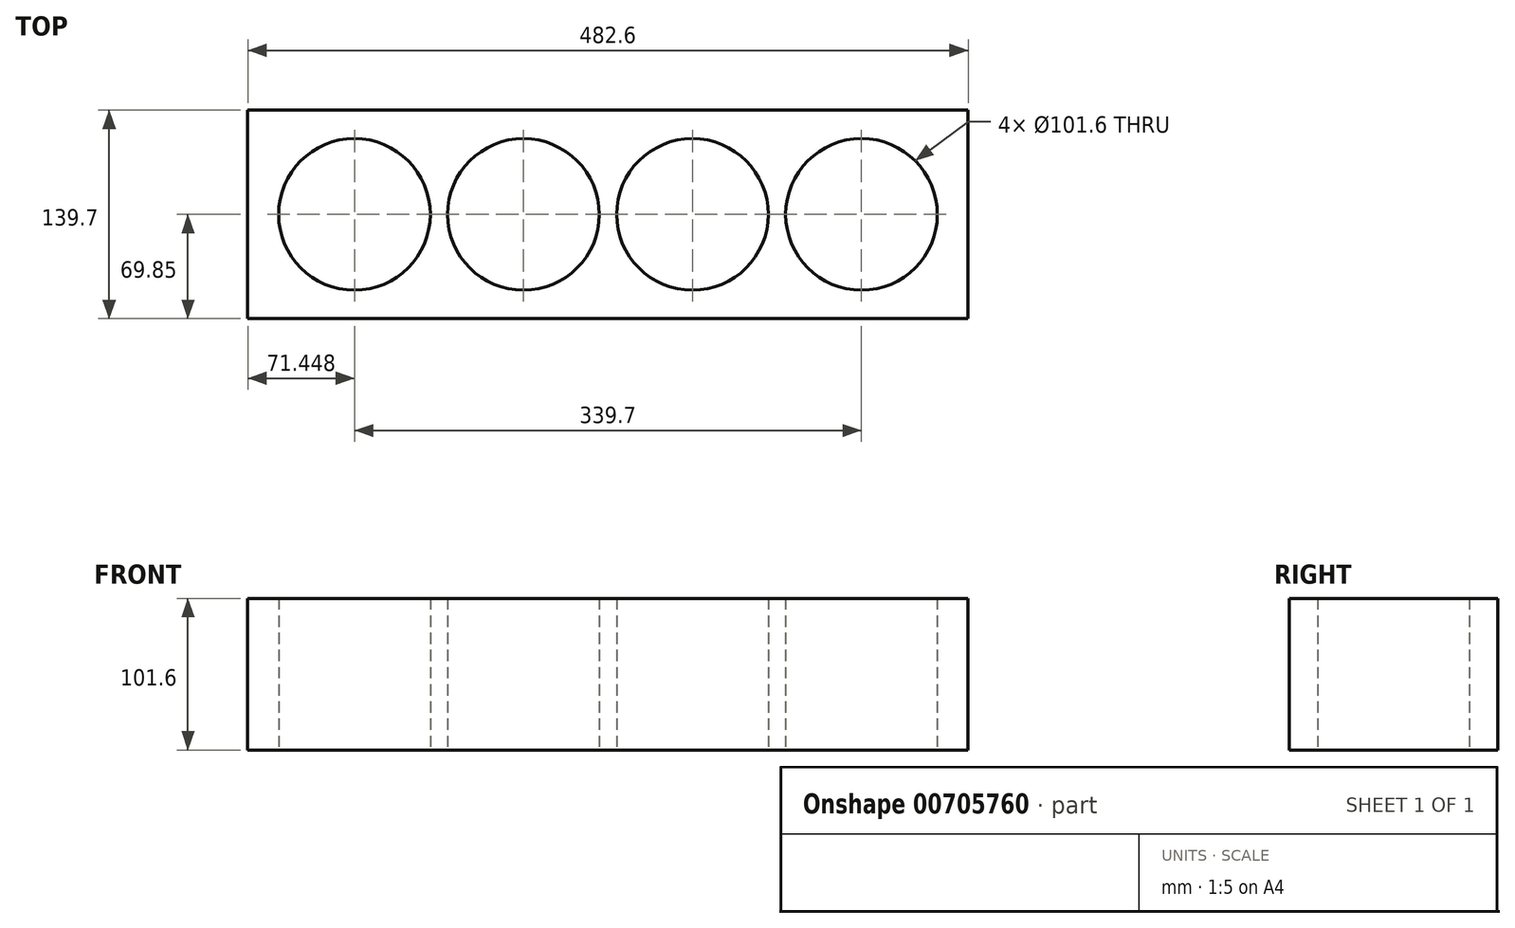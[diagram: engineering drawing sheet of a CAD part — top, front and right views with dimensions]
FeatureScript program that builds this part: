
annotation { "Feature Type Name" : "Feature", "Feature Type Description" : "" }
export const myFeature = defineFeature(function(context is Context, id is Id, definition is map)
    precondition{}
    {
        {
            var Q0;
            Q0=qCreatedBy(makeId("Top.planeOp"),FACE);
            var sketch = newSketch(context, id + "F0", { "sketchPlane" : qUnion([Q0])});
            skCircle(sketch, "E0", {"center": v(-182.01, 0) * mm, "radius": 50.8 * mm});
            skCircle(sketch, "E1.1.0.0", {"center": v(-68.78, 0) * mm, "radius": 50.8 * mm});
            skCircle(sketch, "E1.2.0.0", {"center": v(44.45, 0) * mm, "radius": 50.8 * mm});
            skCircle(sketch, "E1.3.0.0", {"center": v(157.69, 0) * mm, "radius": 50.8 * mm});
            skLineSegment(sketch, "E1.direction1", {"start": v(-182.01, 0) * mm, "end": v(-68.78, 0) * mm, "construction": true});
            skLineSegment(sketch, "E2", {"start": v(-182.01, 0) * mm, "end": v(157.69, 0) * mm, "construction": true});
            skLineSegment(sketch, "E3.bottom", {"start": v(229.14, 69.85) * mm, "end": v(-253.46, 69.85) * mm});
            skLineSegment(sketch, "E3.top", {"start": v(229.14, -69.85) * mm, "end": v(-253.46, -69.85) * mm});
            skLineSegment(sketch, "E3.left", {"start": v(229.14, 69.85) * mm, "end": v(229.14, -69.85) * mm});
            skLineSegment(sketch, "E3.right", {"start": v(-253.46, 69.85) * mm, "end": v(-253.46, -69.85) * mm});
            skPoint(sketch, "E3.middle", {"position": v(-12.16, 0) * mm});
            skSolve(sketch);
        }
        {
            var Q0;
            Q0=makeQuery(id+"F0.imprint","IMPRINT",FACE,{"disambiguationData":[TD([[makeQuery(id+"F0.imprint","IMPRINT",EDGE,{"derivedFrom":sQuery(id+"F0.wireOp",EDGE,"E0")}),-1.0]])]});
            extrude(context, id + "F1", {"entities" : qUnion([Q0]), "depth" : 101.6 * mm, "offsetDistance" : 25.4 * mm});
        }
    });
